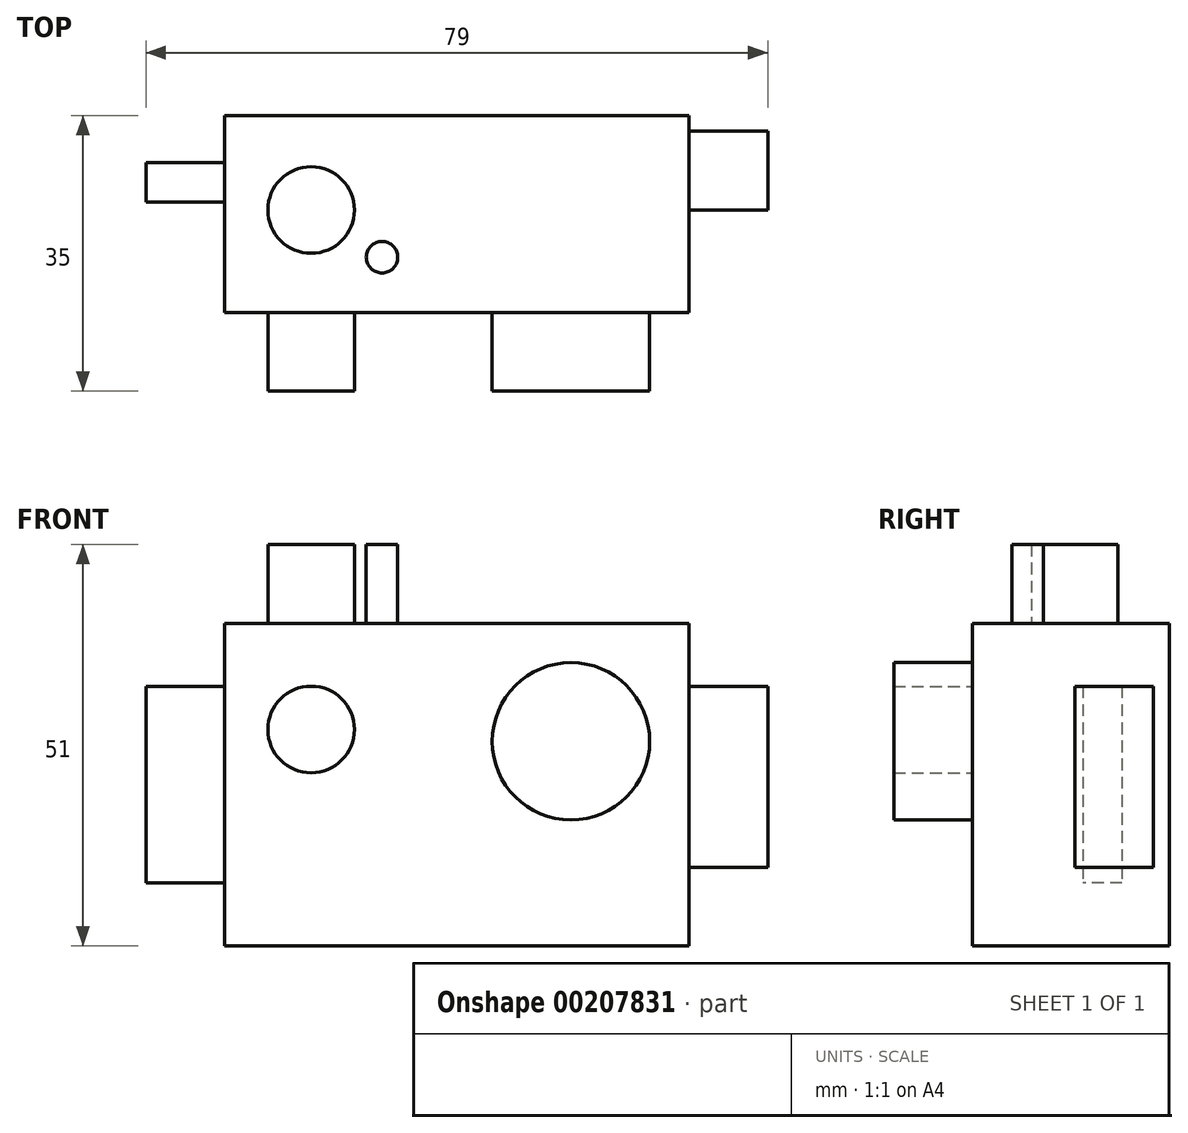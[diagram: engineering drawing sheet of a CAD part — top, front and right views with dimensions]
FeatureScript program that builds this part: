
annotation { "Feature Type Name" : "Feature", "Feature Type Description" : "" }
export const myFeature = defineFeature(function(context is Context, id is Id, definition is map)
    precondition{}
    {
        {
            var Q0;
            Q0=qCreatedBy(makeId("Front.planeOp"),FACE);
            var sketch = newSketch(context, id + "F0", { "sketchPlane" : qUnion([Q0])});
            skLineSegment(sketch, "E0.bottom", {"start": v(-26.52, 21.18) * mm, "end": v(32.48, 21.18) * mm});
            skLineSegment(sketch, "E0.top", {"start": v(-26.52, -19.82) * mm, "end": v(32.48, -19.82) * mm});
            skLineSegment(sketch, "E0.left", {"start": v(-26.52, 21.18) * mm, "end": v(-26.52, -19.82) * mm});
            skLineSegment(sketch, "E0.right", {"start": v(32.48, 21.18) * mm, "end": v(32.48, -19.82) * mm});
            skSolve(sketch);
        }
        {
            var Q0;
            Q0=makeQuery(id+"F0.imprint","IMPRINT",FACE,{"disambiguationData":[TD([[makeQuery(id+"F0.imprint","IMPRINT",EDGE,{"derivedFrom":sQuery(id+"F0.wireOp",EDGE,"E0.bottom")}),-1.0]])]});
            extrude(context, id + "F1", {"entities" : qUnion([Q0]), "depth" : 25 * mm});
        }
        {
            var Q0;
            Q0=makeQuery(id+"F1.opExtrude","CAP_FACE",FACE,{"disambiguationData":[OSD([sQuery(id+"F0.wireOp",EDGE,"E0.bottom"),sQuery(id+"F0.wireOp",EDGE,"E0.top"),sQuery(id+"F0.wireOp",EDGE,"E0.left"),sQuery(id+"F0.wireOp",EDGE,"E0.right")])],"isStart":false});
            var sketch = newSketch(context, id + "F2", { "sketchPlane" : qUnion([Q0])});
            skCircle(sketch, "E1", {"center": v(-15.52, 7.68) * mm, "radius": 5.5 * mm});
            skCircle(sketch, "E2", {"center": v(17.48, 6.18) * mm, "radius": 10 * mm});
            skSolve(sketch);
        }
        {
            var Q0;
            Q0=makeQuery(id+"F2.imprint","IMPRINT",FACE,{"disambiguationData":[TD([[makeQuery(id+"F2.imprint","IMPRINT",EDGE,{"derivedFrom":sQuery(id+"F2.wireOp",EDGE,"E1")}),1.0]])]});
            var Q1;
            Q1=makeQuery(id+"F2.imprint","IMPRINT",FACE,{"disambiguationData":[TD([[makeQuery(id+"F2.imprint","IMPRINT",EDGE,{"derivedFrom":sQuery(id+"F2.wireOp",EDGE,"E2")}),1.0]])]});
            extrude(context, id + "F3", {"entities" : qUnion([Q0, Q1]), "operationType" : NewBodyOperationType.ADD, "depth" : 10 * mm});
        }
        {
            var Q0;
            Q0=makeQuery(id+"F1.opExtrude","SWEPT_FACE",FACE,{"disambiguationData":[OSD([sQuery(id+"F0.wireOp",EDGE,"E0.bottom")])]});
            var sketch = newSketch(context, id + "F4", { "sketchPlane" : qUnion([Q0])});
            skCircle(sketch, "E3", {"center": v(-15.52, -12) * mm, "radius": 5.5 * mm});
            skCircle(sketch, "E4", {"center": v(-6.52, -18) * mm, "radius": 2 * mm});
            skSolve(sketch);
        }
        {
            var Q0;
            Q0=makeQuery(id+"F4.imprint","IMPRINT",FACE,{"disambiguationData":[TD([[makeQuery(id+"F4.imprint","IMPRINT",EDGE,{"derivedFrom":sQuery(id+"F4.wireOp",EDGE,"E4")}),1.0]])]});
            var Q1;
            Q1=makeQuery(id+"F4.imprint","IMPRINT",FACE,{"disambiguationData":[TD([[makeQuery(id+"F4.imprint","IMPRINT",EDGE,{"derivedFrom":sQuery(id+"F4.wireOp",EDGE,"E3")}),1.0]])]});
            extrude(context, id + "F5", {"entities" : qUnion([Q0, Q1]), "operationType" : NewBodyOperationType.ADD, "depth" : 10 * mm});
        }
        {
            var Q0;
            Q0=makeQuery(id+"F1.opExtrude","SWEPT_FACE",FACE,{"disambiguationData":[OSD([sQuery(id+"F0.wireOp",EDGE,"E0.right")])]});
            var sketch = newSketch(context, id + "F6", { "sketchPlane" : qUnion([Q0])});
            skLineSegment(sketch, "E5.bottom", {"start": v(-12, 13.18) * mm, "end": v(-2, 13.18) * mm});
            skLineSegment(sketch, "E5.top", {"start": v(-12, -9.82) * mm, "end": v(-2, -9.82) * mm});
            skLineSegment(sketch, "E5.left", {"start": v(-12, 13.18) * mm, "end": v(-12, -9.82) * mm});
            skLineSegment(sketch, "E5.right", {"start": v(-2, 13.18) * mm, "end": v(-2, -9.82) * mm});
            skSolve(sketch);
        }
        {
            var Q0;
            Q0=makeQuery(id+"F6.imprint","IMPRINT",FACE,{"disambiguationData":[TD([[makeQuery(id+"F6.imprint","IMPRINT",EDGE,{"derivedFrom":sQuery(id+"F6.wireOp",EDGE,"E5.bottom")}),-1.0]])]});
            extrude(context, id + "F7", {"entities" : qUnion([Q0]), "operationType" : NewBodyOperationType.ADD, "depth" : 10 * mm});
        }
        {
            var Q0;
            Q0=makeQuery(id+"F1.opExtrude","SWEPT_FACE",FACE,{"disambiguationData":[OSD([sQuery(id+"F0.wireOp",EDGE,"E0.left")])]});
            var sketch = newSketch(context, id + "F8", { "sketchPlane" : qUnion([Q0])});
            skLineSegment(sketch, "E6.bottom", {"start": v(6, 13.18) * mm, "end": v(11, 13.18) * mm});
            skLineSegment(sketch, "E6.top", {"start": v(6, -11.82) * mm, "end": v(11, -11.82) * mm});
            skLineSegment(sketch, "E6.left", {"start": v(6, 13.18) * mm, "end": v(6, -11.82) * mm});
            skLineSegment(sketch, "E6.right", {"start": v(11, 13.18) * mm, "end": v(11, -11.82) * mm});
            skSolve(sketch);
        }
        {
            var Q0;
            Q0=makeQuery(id+"F8.imprint","IMPRINT",FACE,{"disambiguationData":[TD([[makeQuery(id+"F8.imprint","IMPRINT",EDGE,{"derivedFrom":sQuery(id+"F8.wireOp",EDGE,"E6.bottom")}),-1.0]])]});
            extrude(context, id + "F9", {"entities" : qUnion([Q0]), "operationType" : NewBodyOperationType.ADD, "depth" : 10 * mm});
        }
    });
